# Revit family: 712-7514-001 DN080-700
name_source: partatom
category: Pipe Accessories
units: mm (PartAtom-declared; Revit-internal decimal feet)

## family parameters
Always vertical = Yes
Cut with Voids When Loaded = No
Part Type = Valve - Breaks Into
Round Connector Dimension = Use Diameter
Shared = No
Work Plane-Based = No

## types (19) — shared parameters
1 = 1 mm  [stored 0.00328084 ft]
2 = 2 mm  [stored 0.00656168 ft]
8 = 8 mm  [stored 0.0262467 ft]
DN0080_PN10/16 = 712008075141
DN0100_PN10/16 = 712010075141
DN0125_PN10/16 = 712012575141
DN0150_PN10/16 = 712015075141
DN0200_PN10 = 712020075140
DN0200_PN16 = 712020075141
DN0250_PN10 = 712025075140
DN0250_PN16 = 712025075141
DN0300_PN10 = 712030075140
DN0300_PN16 = 712030075141
DN0350_PN10 = 712035075140
DN0350_PN16 = 712035075141
DN0400_PN10 = 712040075140
DN0400_PN16 = 712040075141
DN0500_PN10 = 712050075140
DN0500_PN16 = 712050075141
DN0600_PN10 = 712060075140
DN0600_PN16 = 712060075141
DN0700_PN16 = 712070075141
Default Elevation = 81 mm
Description_ = AVK DUCTILE IRON FITTING, FLANGE/SOCKET, PN10/16
Search_table = 712-7514-001 DN080-700
Thickness = 6 mm  [stored 0.019685 ft]
URL_product_pages = https://www.avkvalves.com

## per-type parameters (varying)
- DN0080_PN10/16: Body_T=7 mm  [stored 0.0229659 ft]; Bore=40 mm  [stored 0.131234 ft]; C=100 mm; C1=40 mm  [stored 0.131234 ft]; C2=60 mm; DN=80 mm; E=50 mm  [stored 0.164042 ft]; F=65 mm; FL_T=19 mm  [stored 0.062336 ft]; G=73 mm; G1=68 mm; ID=57 mm; ID1=44 mm  [stored 0.144357 ft]; J=8 mm  [stored 0.0262467 ft]; J1=10 mm  [stored 0.0328084 ft]; J2=16 mm  [stored 0.0524934 ft]; L=65 mm; L1=191 mm; Logo=57 mm; OD=100 mm; Raised_dia=66 mm; Raised_dis=3 mm  [stored 0.00984252 ft]; W=71 mm; rad1=6 mm  [stored 0.019685 ft]; radius=14 mm  [stored 0.0459318 ft]
- DN0100_PN10/16: Body_T=7 mm  [stored 0.0229659 ft]; Bore=50 mm  [stored 0.164042 ft]; C=110 mm; C1=44 mm  [stored 0.144357 ft]; C2=66 mm; DN=100 mm; E=63 mm; F=81 mm; FL_T=19 mm  [stored 0.062336 ft]; G=87 mm; G1=80 mm; ID=67 mm; ID1=55 mm  [stored 0.180446 ft]; J=8 mm  [stored 0.0262467 ft]; J1=10 mm  [stored 0.0328084 ft]; J2=16 mm  [stored 0.0524934 ft]; L=65 mm; L1=191 mm; Logo=57 mm; OD=110 mm; Raised_dia=78 mm; Raised_dis=3 mm  [stored 0.00984252 ft]; W=81 mm; rad1=6 mm  [stored 0.019685 ft]; radius=14 mm  [stored 0.0459318 ft]
- DN0125_PN10/16: Body_T=7 mm  [stored 0.0229659 ft]; Bore=63 mm; C=115 mm; C1=46 mm  [stored 0.150919 ft]; C2=69 mm; DN=125 mm; E=75 mm; F=98 mm; FL_T=19 mm  [stored 0.062336 ft]; G=94 mm; G1=86 mm; ID=72 mm; ID1=69 mm; J=8 mm  [stored 0.0262467 ft]; J1=10 mm  [stored 0.0328084 ft]; J2=16 mm  [stored 0.0524934 ft]; L=68 mm; L1=191 mm; Logo=57 mm; OD=125 mm; Raised_dia=92 mm; Raised_dis=3 mm  [stored 0.00984252 ft]; W=91 mm; rad1=6 mm  [stored 0.019685 ft]; radius=14 mm  [stored 0.0459318 ft]
- DN0150_PN10/16: Body_T=7 mm  [stored 0.0229659 ft]; Bore=75 mm; C=120 mm; C1=48 mm  [stored 0.15748 ft]; C2=72 mm; DN=150 mm; E=90 mm; F=117 mm; FL_T=19 mm  [stored 0.062336 ft]; G=100 mm; G1=92 mm; ID=77 mm; ID1=83 mm; J=9 mm  [stored 0.0295276 ft]; J1=11 mm  [stored 0.0360892 ft]; J2=18 mm  [stored 0.0590551 ft]; L=68 mm; L1=200 mm; Logo=60 mm; OD=143 mm; Raised_dia=106 mm; Raised_dis=3 mm  [stored 0.00984252 ft]; W=100 mm; rad1=7 mm  [stored 0.0229659 ft]; radius=14 mm  [stored 0.0459318 ft]
- DN0200_PN10: Body_T=7 mm  [stored 0.0229659 ft]; Bore=100 mm; C=140 mm; C1=56 mm  [stored 0.183727 ft]; C2=84 mm; DN=200 mm; E=118 mm; F=153 mm; FL_T=20 mm  [stored 0.0656168 ft]; G=156 mm; G1=144 mm; ID=120 mm; ID1=110 mm; J=11 mm  [stored 0.0360892 ft]; J1=13 mm; J2=22 mm  [stored 0.0721785 ft]; L=70 mm; L1=213 mm; Logo=64 mm; OD=170 mm; Raised_dia=133 mm; Raised_dis=3 mm  [stored 0.00984252 ft]; W=136 mm; rad1=9 mm  [stored 0.0295276 ft]; radius=15 mm  [stored 0.0492126 ft]
- DN0200_PN16: Body_T=7 mm  [stored 0.0229659 ft]; Bore=100 mm; C=140 mm; C1=56 mm  [stored 0.183727 ft]; C2=84 mm; DN=200 mm; E=118 mm; F=153 mm; FL_T=20 mm  [stored 0.0656168 ft]; G=156 mm; G1=144 mm; ID=120 mm; ID1=110 mm; J=11 mm  [stored 0.0360892 ft]; J1=13 mm; J2=22 mm  [stored 0.0721785 ft]; L=70 mm; L1=213 mm; Logo=64 mm; OD=170 mm; Raised_dia=133 mm; Raised_dis=3 mm  [stored 0.00984252 ft]; W=136 mm; rad1=9 mm  [stored 0.0295276 ft]; radius=15 mm  [stored 0.0492126 ft]
- DN0250_PN10: Body_T=8 mm  [stored 0.0262467 ft]; Bore=125 mm; C=150 mm; C1=60 mm; C2=90 mm; DN=250 mm; E=145 mm; F=189 mm; FL_T=22 mm  [stored 0.0721785 ft]; G=195 mm; G1=180 mm; ID=150 mm; ID1=138 mm; J=12 mm  [stored 0.0393701 ft]; J1=14 mm  [stored 0.0459318 ft]; J2=24 mm  [stored 0.0787402 ft]; L=73 mm; L1=224 mm; Logo=67 mm; OD=198 mm; Raised_dia=160 mm; Raised_dis=3 mm  [stored 0.00984252 ft]; W=150 mm; rad1=10 mm  [stored 0.0328084 ft]; radius=17 mm  [stored 0.0557743 ft]
- DN0250_PN16: Body_T=8 mm  [stored 0.0262467 ft]; Bore=125 mm; C=150 mm; C1=60 mm; C2=90 mm; DN=250 mm; E=145 mm; F=189 mm; FL_T=22 mm  [stored 0.0721785 ft]; G=195 mm; G1=180 mm; ID=150 mm; ID1=138 mm; J=12 mm  [stored 0.0393701 ft]; J1=14 mm  [stored 0.0459318 ft]; J2=24 mm  [stored 0.0787402 ft]; L=73 mm; L1=224 mm; Logo=67 mm; OD=203 mm; Raised_dia=160 mm; Raised_dis=3 mm  [stored 0.00984252 ft]; W=150 mm; rad1=10 mm  [stored 0.0328084 ft]; radius=17 mm  [stored 0.0557743 ft]
- DN0300_PN10: Body_T=8 mm  [stored 0.0262467 ft]; Bore=150 mm; C=160 mm; C1=64 mm; C2=96 mm; DN=300 mm; E=174 mm; F=226 mm; FL_T=25 mm  [stored 0.082021 ft]; G=228 mm; G1=210 mm; ID=175 mm; ID1=165 mm; J=13 mm; J1=16 mm  [stored 0.0524934 ft]; J2=26 mm; L=75 mm; L1=230 mm; Logo=69 mm; OD=223 mm; Raised_dia=185 mm; Raised_dis=4 mm  [stored 0.0131234 ft]; W=175 mm; rad1=10 mm  [stored 0.0328084 ft]; radius=19 mm  [stored 0.062336 ft]
- DN0300_PN16: Body_T=8 mm  [stored 0.0262467 ft]; Bore=150 mm; C=160 mm; C1=64 mm; C2=96 mm; DN=300 mm; E=174 mm; F=226 mm; FL_T=25 mm  [stored 0.082021 ft]; G=228 mm; G1=210 mm; ID=175 mm; ID1=165 mm; J=13 mm; J1=16 mm  [stored 0.0524934 ft]; J2=26 mm; L=75 mm; L1=230 mm; Logo=69 mm; OD=230 mm; Raised_dia=185 mm; Raised_dis=4 mm  [stored 0.0131234 ft]; W=175 mm; rad1=10 mm  [stored 0.0328084 ft]; radius=19 mm  [stored 0.062336 ft]
- DN0350_PN10: Body_T=9 mm  [stored 0.0295276 ft]; Bore=175 mm; C=160 mm; C1=64 mm; C2=96 mm; DN=350 mm; E=210 mm; F=273 mm; FL_T=25 mm  [stored 0.082021 ft]; G=257 mm; G1=238 mm; ID=198 mm; ID1=193 mm; J=14 mm  [stored 0.0459318 ft]; J1=17 mm  [stored 0.0557743 ft]; J2=28 mm  [stored 0.0918635 ft]; L=78 mm; L1=233 mm; Logo=70 mm; OD=253 mm; Raised_dia=215 mm; Raised_dis=4 mm  [stored 0.0131234 ft]; W=217 mm; rad1=11 mm  [stored 0.0360892 ft]; radius=19 mm  [stored 0.062336 ft]
- DN0350_PN16: Body_T=9 mm  [stored 0.0295276 ft]; Bore=175 mm; C=160 mm; C1=64 mm; C2=96 mm; DN=350 mm; E=210 mm; F=273 mm; FL_T=27 mm  [stored 0.0885827 ft]; G=257 mm; G1=238 mm; ID=198 mm; ID1=193 mm; J=14 mm  [stored 0.0459318 ft]; J1=17 mm  [stored 0.0557743 ft]; J2=28 mm  [stored 0.0918635 ft]; L=78 mm; L1=233 mm; Logo=70 mm; OD=260 mm; Raised_dia=215 mm; Raised_dis=4 mm  [stored 0.0131234 ft]; W=217 mm; rad1=11 mm  [stored 0.0360892 ft]; radius=20 mm  [stored 0.0656168 ft]
- DN0400_PN10: Body_T=10 mm  [stored 0.0328084 ft]; Bore=200 mm; C=170 mm; C1=68 mm; C2=102 mm; DN=400 mm; E=250 mm; F=325 mm; FL_T=25 mm  [stored 0.082021 ft]; G=283 mm; G1=262 mm; ID=218 mm; ID1=220 mm; J=15 mm  [stored 0.0492126 ft]; J1=18 mm  [stored 0.0590551 ft]; J2=30 mm  [stored 0.0984252 ft]; L=80 mm; L1=234 mm; Logo=70 mm; OD=283 mm; Raised_dia=240 mm; Raised_dis=4 mm  [stored 0.0131234 ft]; W=250 mm; rad1=12 mm  [stored 0.0393701 ft]; radius=19 mm  [stored 0.062336 ft]
- DN0400_PN16: Body_T=10 mm  [stored 0.0328084 ft]; Bore=200 mm; C=170 mm; C1=68 mm; C2=102 mm; DN=400 mm; E=250 mm; F=325 mm; FL_T=28 mm  [stored 0.0918635 ft]; G=283 mm; G1=262 mm; ID=218 mm; ID1=220 mm; J=15 mm  [stored 0.0492126 ft]; J1=18 mm  [stored 0.0590551 ft]; J2=30 mm  [stored 0.0984252 ft]; L=80 mm; L1=234 mm; Logo=70 mm; OD=290 mm; Raised_dia=240 mm; Raised_dis=4 mm  [stored 0.0131234 ft]; W=250 mm; rad1=12 mm  [stored 0.0393701 ft]; radius=21 mm  [stored 0.0688976 ft]
- DN0500_PN10: Body_T=11 mm  [stored 0.0360892 ft]; Bore=250 mm; C=175 mm; C1=70 mm; C2=105 mm; DN=500 mm; E=282 mm; F=367 mm; FL_T=27 mm  [stored 0.0885827 ft]; G=351 mm; G1=324 mm; ID=270 mm; ID1=275 mm; J=16 mm  [stored 0.0524934 ft]; J1=19 mm  [stored 0.062336 ft]; J2=32 mm  [stored 0.104987 ft]; L=85 mm; L1=251 mm; Logo=75 mm; OD=335 mm; Raised_dia=291 mm; Raised_dis=4 mm  [stored 0.0131234 ft]; W=302 mm; rad1=13 mm; radius=20 mm  [stored 0.0656168 ft]
- DN0500_PN16: Body_T=11 mm  [stored 0.0360892 ft]; Bore=250 mm; C=175 mm; C1=70 mm; C2=105 mm; DN=500 mm; E=282 mm; F=367 mm; FL_T=32 mm  [stored 0.104987 ft]; G=351 mm; G1=324 mm; ID=270 mm; ID1=275 mm; J=16 mm  [stored 0.0524934 ft]; J1=19 mm  [stored 0.062336 ft]; J2=32 mm  [stored 0.104987 ft]; L=85 mm; L1=251 mm; Logo=75 mm; OD=358 mm; Raised_dia=305 mm; Raised_dis=4 mm  [stored 0.0131234 ft]; W=302 mm; rad1=13 mm; radius=24 mm  [stored 0.0787402 ft]
- DN0600_PN10: Body_T=12 mm  [stored 0.0393701 ft]; Bore=300 mm; C=185 mm; C1=74 mm; C2=111 mm; DN=600 mm; E=336 mm; F=436 mm; FL_T=30 mm  [stored 0.0984252 ft]; G=415 mm; G1=383 mm; ID=319 mm; ID1=330 mm; J=17 mm  [stored 0.0557743 ft]; J1=20 mm  [stored 0.0656168 ft]; J2=34 mm; L=90 mm; L1=266 mm; Logo=80 mm; OD=390 mm; Raised_dia=341 mm; Raised_dis=5 mm  [stored 0.0164042 ft]; W=349 mm; rad1=14 mm  [stored 0.0459318 ft]; radius=23 mm
- DN0600_PN16: Body_T=12 mm  [stored 0.0393701 ft]; Bore=300 mm; C=185 mm; C1=74 mm; C2=111 mm; DN=600 mm; E=336 mm; F=436 mm; FL_T=36 mm  [stored 0.11811 ft]; G=415 mm; G1=383 mm; ID=319 mm; ID1=330 mm; J=17 mm  [stored 0.0557743 ft]; J1=20 mm  [stored 0.0656168 ft]; J2=34 mm; L=90 mm; L1=266 mm; Logo=80 mm; OD=420 mm; Raised_dia=360 mm; Raised_dis=4 mm  [stored 0.0131234 ft]; W=349 mm; rad1=14 mm  [stored 0.0459318 ft]; radius=27 mm  [stored 0.0885827 ft]
- DN0700_PN16: Body_T=14 mm  [stored 0.0459318 ft]; Bore=350 mm; C=157 mm; C1=63 mm; C2=94 mm; DN=700 mm; E=415 mm; F=540 mm; FL_T=33 mm; G=484 mm; G1=447 mm; ID=373 mm; ID1=385 mm; J=20 mm  [stored 0.0656168 ft]; J1=24 mm  [stored 0.0787402 ft]; J2=40 mm  [stored 0.131234 ft]; L=95 mm; L1=340 mm; Logo=102 mm; OD=448 mm; Raised_dia=397 mm; Raised_dis=5 mm  [stored 0.0164042 ft]; W=413 mm; rad1=16 mm  [stored 0.0524934 ft]; radius=24 mm  [stored 0.0787402 ft]

note: [stored X ft] marks values corroborated as IEEE doubles in the binary element streams (Revit-internal decimal feet)

## geometry (parser evidence)
native form markers: Sweep x4
no freeform markers — native parametric forms only
